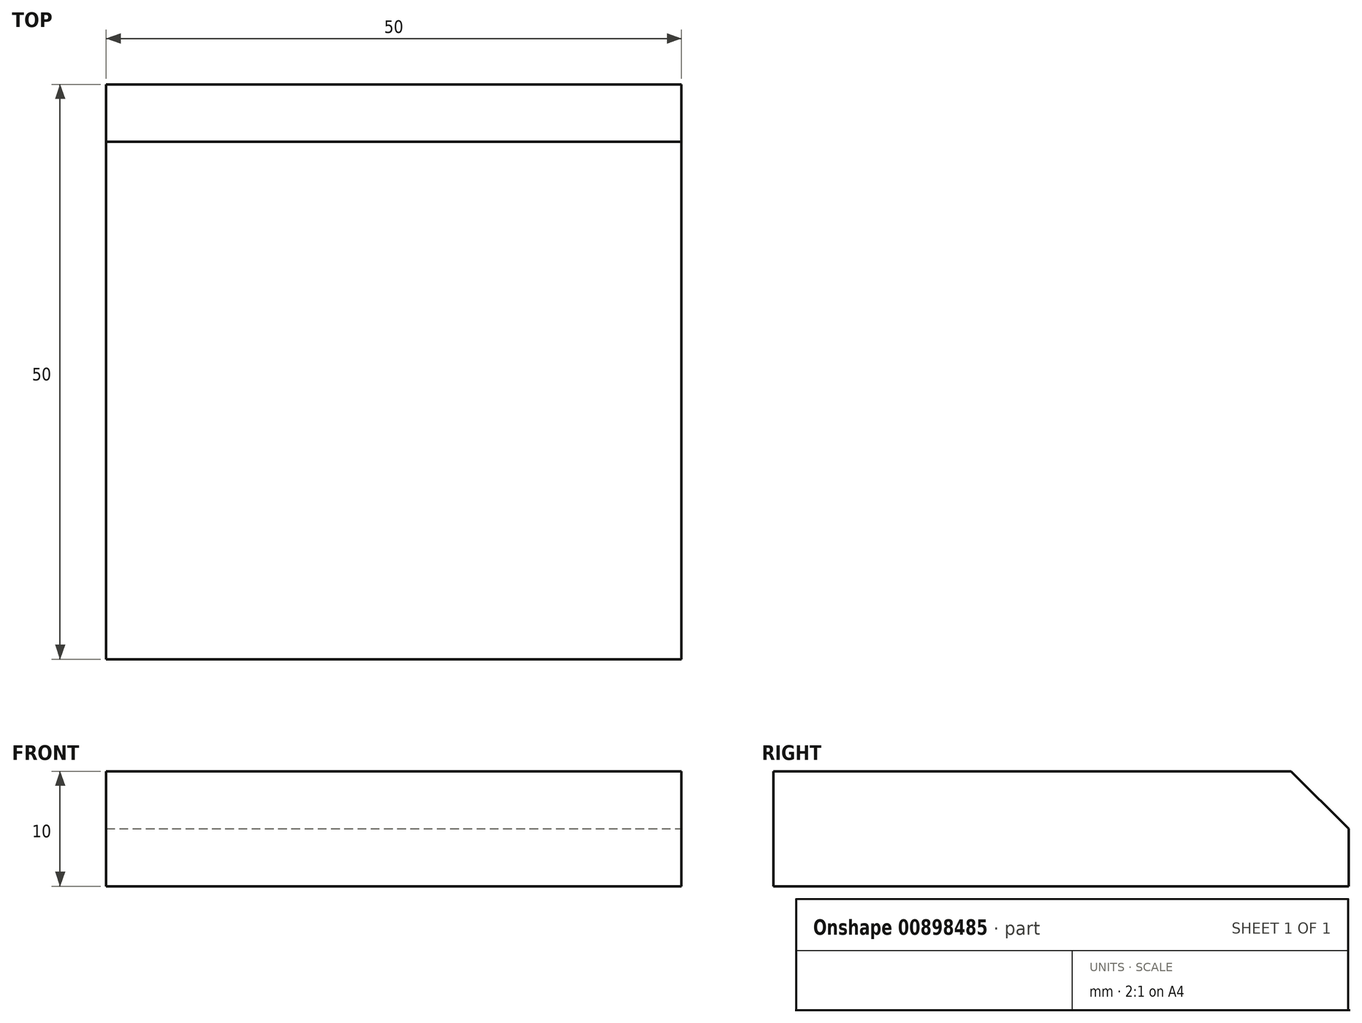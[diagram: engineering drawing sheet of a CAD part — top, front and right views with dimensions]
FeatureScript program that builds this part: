
annotation { "Feature Type Name" : "Feature", "Feature Type Description" : "" }
export const myFeature = defineFeature(function(context is Context, id is Id, definition is map)
    precondition{}
    {
        {
            var Q0;
            Q0=qCreatedBy(makeId("Top.planeOp"),FACE);
            var sketch = newSketch(context, id + "F0", { "sketchPlane" : qUnion([Q0])});
            skLineSegment(sketch, "E0.bottom", {"start": v(-22.63, -20.24) * mm, "end": v(27.37, -20.24) * mm});
            skLineSegment(sketch, "E0.top", {"start": v(-22.63, 29.76) * mm, "end": v(27.37, 29.76) * mm});
            skLineSegment(sketch, "E0.left", {"start": v(-22.63, -20.24) * mm, "end": v(-22.63, 29.76) * mm});
            skLineSegment(sketch, "E0.right", {"start": v(27.37, -20.24) * mm, "end": v(27.37, 29.76) * mm});
            skSolve(sketch);
        }
        {
            var Q0;
            Q0 = qSketchRegion(id + "F0", true);
            extrude(context, id + "F1", {"entities" : qUnion([Q0]), "depth" : 10 * mm, "offsetDistance" : 25 * mm});
        }
        {
            var Q0;
            Q0=makeQuery(id+"F1.opExtrude","CAP_EDGE",EDGE,{"disambiguationData":[OSD([sQuery(id+"F0.wireOp",EDGE,"E0.top")])],"isStart":false});
            chamfer(context, id + "F2", {"entities" : qUnion([Q0]), "width" : 5 * mm, "tangentPropagation" : true});
        }
    });
